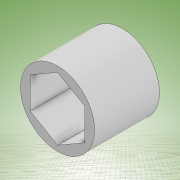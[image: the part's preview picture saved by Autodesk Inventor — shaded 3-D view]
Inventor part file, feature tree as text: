
AUTODESK INVENTOR PART (.ipt)
format: ipt  version: 2022 (Build 260153000, 153)  size: 117,760 bytes
history: native  units: mm
features: other x1, extrude x1, sketch x1
ambient origin geometry x8: Origin, YZ Plane, XZ Plane, XY Plane, X Axis, Y Axis, Z Axis, Center Point
bodies: Body1 (feature_tree)
feature tree (3):
  other  "Sólido1"
  extrude  "Extrusión1"  Depth=5.9mm
  sketch  "Boceto1"  dims[d0=8.0mm d1=5.9mm d2=7.0mm d3=0.0mm]
